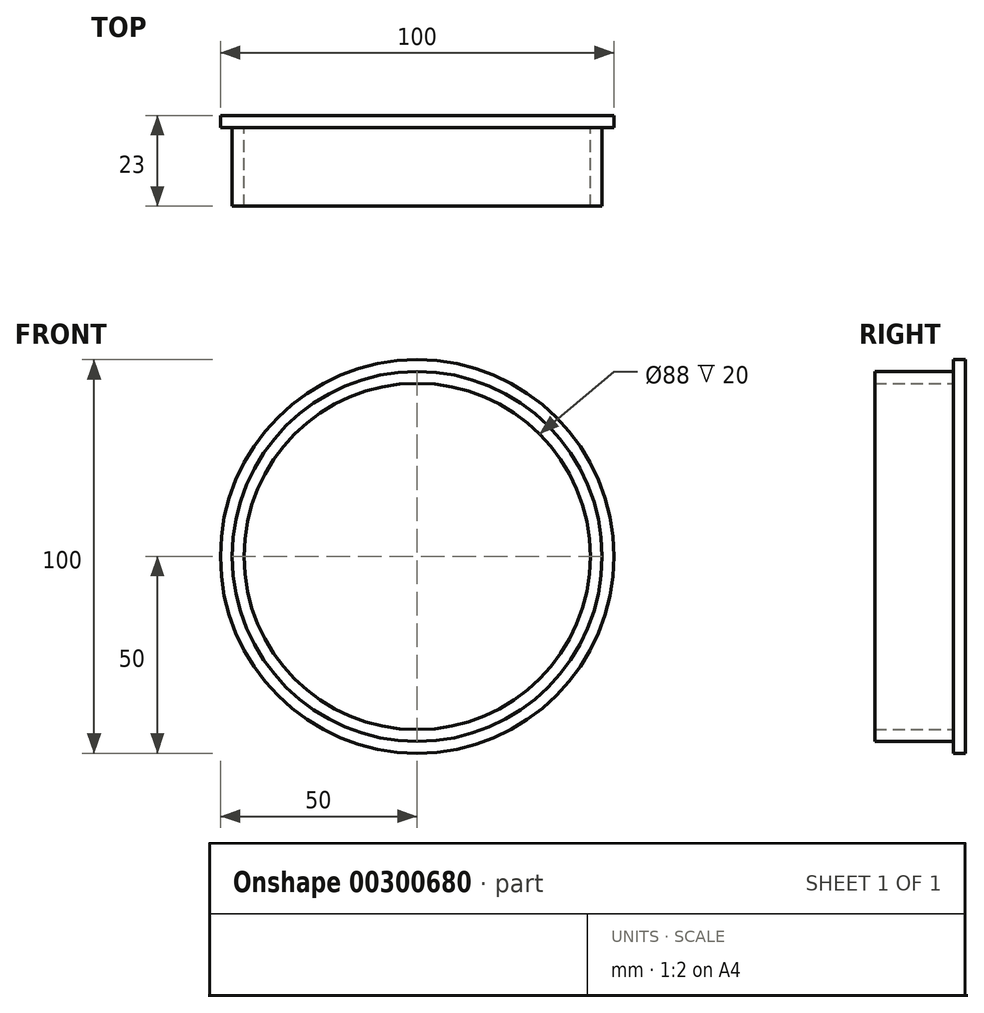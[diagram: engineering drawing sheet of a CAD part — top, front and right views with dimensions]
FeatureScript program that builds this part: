
annotation { "Feature Type Name" : "Feature", "Feature Type Description" : "" }
export const myFeature = defineFeature(function(context is Context, id is Id, definition is map)
    precondition{}
    {
        {
            var Q0;
            Q0=qCreatedBy(makeId("Front.planeOp"),FACE);
            var sketch = newSketch(context, id + "F0", { "sketchPlane" : qUnion([Q0])});
            skCircle(sketch, "E0", {"center": v(0, 0) * mm, "radius": 50 * mm});
            skSolve(sketch);
        }
        {
            var Q0;
            Q0 = qSketchRegion(id + "F0", true);
            extrude(context, id + "F1", {"entities" : qUnion([Q0]), "depth" : 3 * mm});
        }
        {
            var Q0;
            Q0=makeQuery(id+"F1.opExtrude","CAP_FACE",FACE,{"disambiguationData":[OSD([sQuery(id+"F0.wireOp",EDGE,"E0")])],"isStart":false});
            var sketch = newSketch(context, id + "F2", { "sketchPlane" : qUnion([Q0])});
            skCircle(sketch, "E1", {"center": v(0, 0) * mm, "radius": 47 * mm});
            skCircle(sketch, "E2", {"center": v(0, 0) * mm, "radius": 44 * mm});
            skSolve(sketch);
        }
        {
            var Q0;
            Q0=makeQuery(id+"F2.imprint","IMPRINT",FACE,{"disambiguationData":[TD([[makeQuery(id+"F2.imprint","IMPRINT",EDGE,{"derivedFrom":sQuery(id+"F2.wireOp",EDGE,"E1")}),1.0]])]});
            extrude(context, id + "F3", {"entities" : qUnion([Q0]), "operationType" : NewBodyOperationType.ADD, "depth" : 20 * mm});
        }
    });
